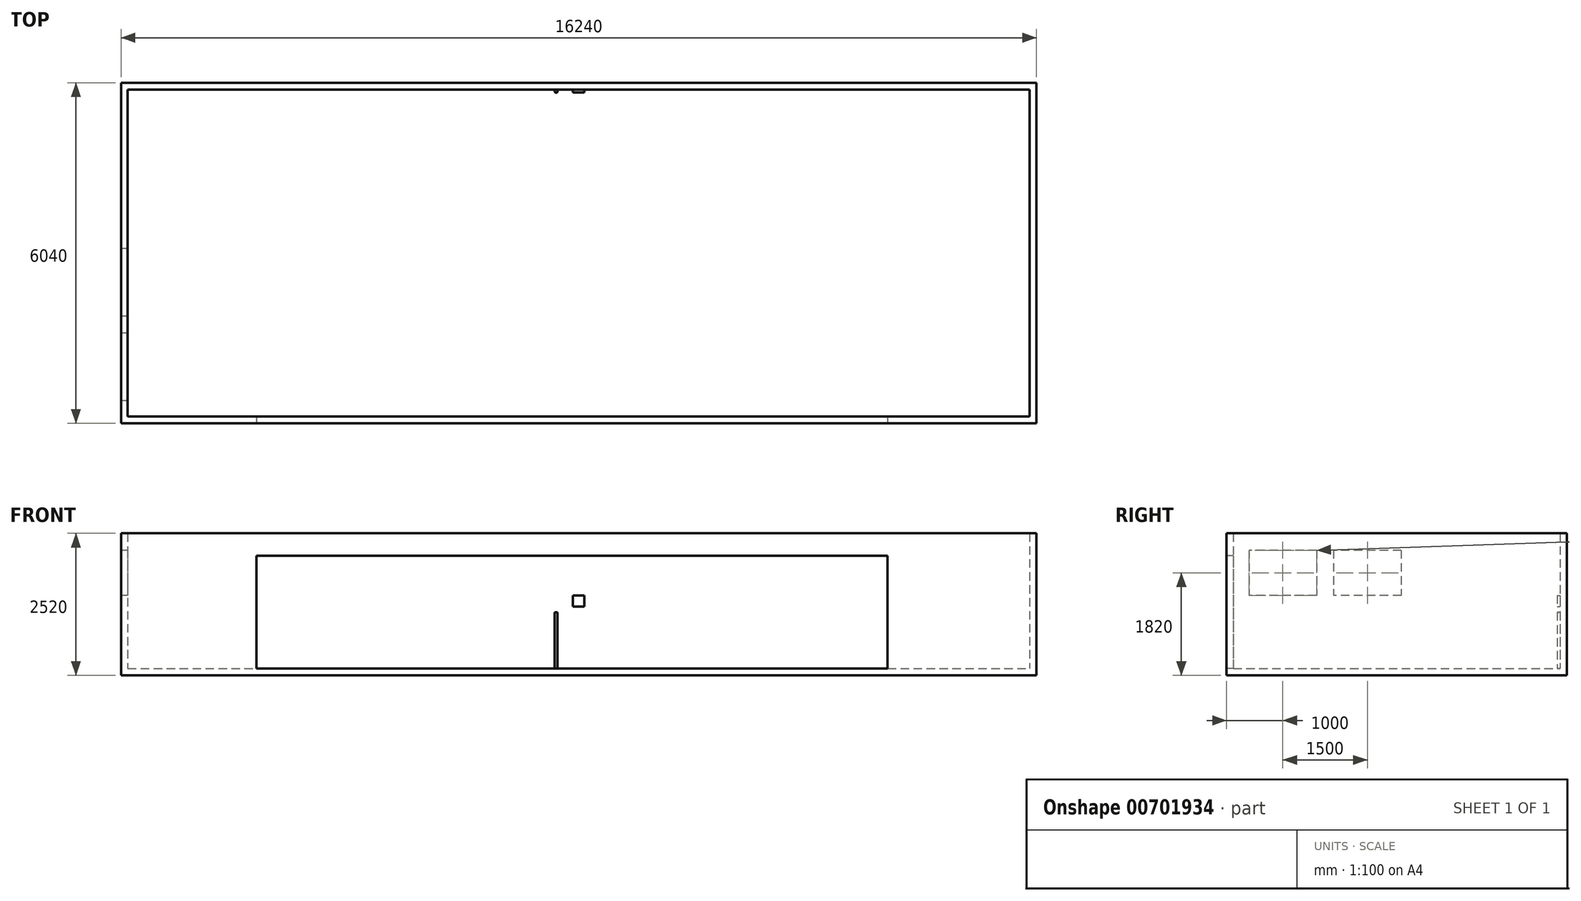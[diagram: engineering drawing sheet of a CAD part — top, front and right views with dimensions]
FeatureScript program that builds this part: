
annotation { "Feature Type Name" : "Feature", "Feature Type Description" : "" }
export const myFeature = defineFeature(function(context is Context, id is Id, definition is map)
    precondition{}
    {
        {
            var Q0;
            Q0=qCreatedBy(makeId("Top.planeOp"),FACE);
            var sketch = newSketch(context, id + "F0", { "sketchPlane" : qUnion([Q0])});
            skLineSegment(sketch, "E0.bottom", {"start": v(0, 0) * mm, "end": v(16000, 0) * mm});
            skLineSegment(sketch, "E0.top", {"start": v(0, 5800) * mm, "end": v(16000, 5800) * mm});
            skLineSegment(sketch, "E0.left", {"start": v(0, 0) * mm, "end": v(0, 5800) * mm});
            skLineSegment(sketch, "E0.right", {"start": v(16000, 0) * mm, "end": v(16000, 5800) * mm});
            skSolve(sketch);
        }
        {
            var Q0;
            Q0=makeQuery(id+"F0.imprint","IMPRINT",FACE,{"disambiguationData":[TD([[makeQuery(id+"F0.imprint","IMPRINT",EDGE,{"derivedFrom":sQuery(id+"F0.wireOp",EDGE,"E0.bottom")}),1.0]])]});
            extrude(context, id + "F1", {"entities" : qUnion([Q0]), "depth" : 2400 * mm, "offsetDistance" : 25 * mm});
        }
        {
            var Q0;
            Q0=makeQuery(id+"F1.opExtrude","CAP_FACE",FACE,{"disambiguationData":[OSD([sQuery(id+"F0.wireOp",EDGE,"E0.bottom"),sQuery(id+"F0.wireOp",EDGE,"E0.top"),sQuery(id+"F0.wireOp",EDGE,"E0.left"),sQuery(id+"F0.wireOp",EDGE,"E0.right")])],"isStart":false});
            shell(context, id + "F2", {"entities" : qUnion([Q0]), "thickness" : 120 * mm, "oppositeDirection" : true});
        }
        {
            var Q0;
            Q0=makeQuery(id+"F1.opExtrude","SWEPT_FACE",FACE,{"disambiguationData":[OSD([sQuery(id+"F0.wireOp",EDGE,"E0.left")])]});
            var sketch = newSketch(context, id + "F3", { "sketchPlane" : qUnion([Q0])});
            skLineSegment(sketch, "E1.bottom", {"start": v(-2980, 2100) * mm, "end": v(-1780, 2100) * mm});
            skLineSegment(sketch, "E1.top", {"start": v(-2980, 1300) * mm, "end": v(-1780, 1300) * mm});
            skLineSegment(sketch, "E1.left", {"start": v(-2980, 2100) * mm, "end": v(-2980, 1300) * mm});
            skLineSegment(sketch, "E1.right", {"start": v(-1780, 2100) * mm, "end": v(-1780, 1300) * mm});
            skLineSegment(sketch, "E2.bottom", {"start": v(-1480, 2100) * mm, "end": v(-280, 2100) * mm});
            skLineSegment(sketch, "E2.top", {"start": v(-1480, 1300) * mm, "end": v(-280, 1300) * mm});
            skLineSegment(sketch, "E2.left", {"start": v(-1480, 2100) * mm, "end": v(-1480, 1300) * mm});
            skLineSegment(sketch, "E2.right", {"start": v(-280, 2100) * mm, "end": v(-280, 1300) * mm});
            skSolve(sketch);
        }
        {
            var Q0;
            Q0=makeQuery(id+"F3.imprint","IMPRINT",FACE,{"disambiguationData":[TD([[makeQuery(id+"F3.imprint","IMPRINT",EDGE,{"derivedFrom":sQuery(id+"F3.wireOp",EDGE,"E1.bottom")}),-1.0]])]});
            var Q1;
            Q1=makeQuery(id+"F3.imprint","IMPRINT",FACE,{"disambiguationData":[TD([[makeQuery(id+"F3.imprint","IMPRINT",EDGE,{"derivedFrom":sQuery(id+"F3.wireOp",EDGE,"E2.bottom")}),-1.0]])]});
            extrude(context, id + "F4", {"entities" : qUnion([Q0, Q1]), "operationType" : NewBodyOperationType.REMOVE, "oppositeDirection" : true, "depth" : 120 * mm, "offsetDistance" : 25 * mm});
        }
        {
            var Q0;
            Q0=makeQuery(id+"F1.opExtrude","SWEPT_FACE",FACE,{"disambiguationData":[OSD([sQuery(id+"F0.wireOp",EDGE,"E0.bottom")])]});
            var sketch = newSketch(context, id + "F5", { "sketchPlane" : qUnion([Q0])});
            skLineSegment(sketch, "E3.bottom", {"start": v(2280, 0) * mm, "end": v(5080, 0) * mm});
            skLineSegment(sketch, "E3.top", {"start": v(2280, 2000) * mm, "end": v(5080, 2000) * mm});
            skLineSegment(sketch, "E3.left", {"start": v(2280, 0) * mm, "end": v(2280, 2000) * mm});
            skLineSegment(sketch, "E3.right", {"start": v(5080, 0) * mm, "end": v(5080, 2000) * mm});
            skLineSegment(sketch, "E4.bottom", {"start": v(5080, 2000) * mm, "end": v(7880, 2000) * mm});
            skLineSegment(sketch, "E4.top", {"start": v(5080, 0) * mm, "end": v(7880, 0) * mm});
            skLineSegment(sketch, "E4.left", {"start": v(5080, 2000) * mm, "end": v(5080, 0) * mm});
            skLineSegment(sketch, "E4.right", {"start": v(7880, 2000) * mm, "end": v(7880, 0) * mm});
            skLineSegment(sketch, "E5.bottom", {"start": v(7880, 0) * mm, "end": v(10680, 0) * mm});
            skLineSegment(sketch, "E5.top", {"start": v(7880, 2000) * mm, "end": v(10680, 2000) * mm});
            skLineSegment(sketch, "E5.left", {"start": v(7880, 0) * mm, "end": v(7880, 2000) * mm});
            skLineSegment(sketch, "E5.right", {"start": v(10680, 0) * mm, "end": v(10680, 2000) * mm});
            skLineSegment(sketch, "E6.bottom", {"start": v(10680, 2000) * mm, "end": v(13480, 2000) * mm});
            skLineSegment(sketch, "E6.top", {"start": v(10680, 0) * mm, "end": v(13480, 0) * mm});
            skLineSegment(sketch, "E6.left", {"start": v(10680, 2000) * mm, "end": v(10680, 0) * mm});
            skLineSegment(sketch, "E6.right", {"start": v(13480, 2000) * mm, "end": v(13480, 0) * mm});
            skSolve(sketch);
        }
        {
            var Q0;
            Q0=makeQuery(id+"F5.imprint","IMPRINT",FACE,{"disambiguationData":[TD([[makeQuery(id+"F5.imprint","IMPRINT",EDGE,{"derivedFrom":sQuery(id+"F5.wireOp",EDGE,"E3.bottom")}),1.0]])]});
            var Q1;
            Q1=makeQuery(id+"F5.imprint","IMPRINT",FACE,{"disambiguationData":[TD([[makeQuery(id+"F5.imprint","IMPRINT",EDGE,{"derivedFrom":sQuery(id+"F5.wireOp",EDGE,"E4.bottom")}),-1.0]])]});
            var Q2;
            Q2=makeQuery(id+"F5.imprint","IMPRINT",FACE,{"disambiguationData":[TD([[makeQuery(id+"F5.imprint","IMPRINT",EDGE,{"derivedFrom":sQuery(id+"F5.wireOp",EDGE,"E5.bottom")}),1.0]])]});
            var Q3;
            Q3=makeQuery(id+"F5.imprint","IMPRINT",FACE,{"disambiguationData":[TD([[makeQuery(id+"F5.imprint","IMPRINT",EDGE,{"derivedFrom":sQuery(id+"F5.wireOp",EDGE,"E6.bottom")}),-1.0]])]});
            extrude(context, id + "F6", {"entities" : qUnion([Q0, Q1, Q2, Q3]), "operationType" : NewBodyOperationType.REMOVE, "oppositeDirection" : true, "depth" : 1200 * mm, "offsetDistance" : 25 * mm});
        }
        {
            var Q0;
            Q0=makeQuery(id+"F2.opShell","OFFSET_FACE",FACE,{"disambiguationData":[OSD([sQuery(id+"F0.wireOp",EDGE,"E0.top")])]});
            var sketch = newSketch(context, id + "F7", { "sketchPlane" : qUnion([Q0])});
            skLineSegment(sketch, "E7.bottom", {"start": v(7900, 1300) * mm, "end": v(8100, 1300) * mm});
            skLineSegment(sketch, "E7.top", {"start": v(7900, 1100) * mm, "end": v(8100, 1100) * mm});
            skLineSegment(sketch, "E7.left", {"start": v(7900, 1300) * mm, "end": v(7900, 1100) * mm});
            skLineSegment(sketch, "E7.right", {"start": v(8100, 1300) * mm, "end": v(8100, 1100) * mm});
            skSolve(sketch);
        }
        {
            var Q0;
            Q0=makeQuery(id+"F7.imprint","IMPRINT",FACE,{"disambiguationData":[TD([[makeQuery(id+"F7.imprint","IMPRINT",EDGE,{"derivedFrom":sQuery(id+"F7.wireOp",EDGE,"E7.bottom")}),-1.0]])]});
            extrude(context, id + "F8", {"entities" : qUnion([Q0]), "depth" : 50 * mm, "offsetDistance" : 25 * mm});
        }
        {
            var Q0;
            Q0=makeQuery(id+"F6.boolean.opBoolean","MERGE",FACE,{"derivedFrom":[makeQuery(id+"Fwlyr2kBqkPmsQg_1.boolean.opBoolean","MERGE",FACE,{"derivedFrom":[makeQuery(id+"F2.opShell","OFFSET_FACE",FACE,{"disambiguationData":[OSD([sQuery(id+"F0.wireOp",EDGE,"E0.bottom"),sQuery(id+"F0.wireOp",EDGE,"E0.top"),sQuery(id+"F0.wireOp",EDGE,"E0.left"),sQuery(id+"F0.wireOp",EDGE,"E0.right")])]}),makeQuery(id+"Fwlyr2kBqkPmsQg_1.opExtrude","SWEPT_FACE",FACE,{"disambiguationData":[OSD([sQuery(id+"FmUlREnximWoM3x_1.wireOp",EDGE,"xCv455yZ-y8dr-FfYR-MrYS-eXy8WkbMVEua.bottom")])]})]}),makeQuery(id+"F6.opExtrude","SWEPT_FACE",FACE,{"disambiguationData":[OSD([sQuery(id+"F5.wireOp",EDGE,"E3.bottom"),sQuery(id+"F5.wireOp",EDGE,"E4.top"),sQuery(id+"F5.wireOp",EDGE,"E5.bottom"),sQuery(id+"F5.wireOp",EDGE,"E6.top")])]})]});
            var sketch = newSketch(context, id + "F9", { "sketchPlane" : qUnion([Q0])});
            skCircle(sketch, "E8", {"center": v(7600, 5770) * mm, "radius": 25 * mm});
            skSolve(sketch);
        }
        {
            var Q0;
            Q0=makeQuery(id+"F9.imprint","IMPRINT",FACE,{"disambiguationData":[TD([[makeQuery(id+"F9.imprint","IMPRINT",EDGE,{"derivedFrom":sQuery(id+"F9.wireOp",EDGE,"E8")}),1.0]])]});
            extrude(context, id + "F10", {"entities" : qUnion([Q0]), "depth" : 1000 * mm, "offsetDistance" : 25 * mm});
        }
    });
